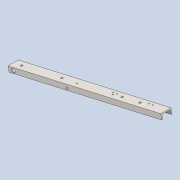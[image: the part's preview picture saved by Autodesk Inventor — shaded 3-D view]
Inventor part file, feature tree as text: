
AUTODESK INVENTOR PART (.ipt)
format: ipt  version: 2021 (Build 250183000, 183)  size: 134,144 bytes
history: native  units: mm
features: other x1, extrude x1, sketch x1, imported_body x1
ambient origin geometry x8: Origin, YZ Plane, XZ Plane, XY Plane, X Axis, Y Axis, Z Axis, Center Point
bodies: Body1 (feature_tree)
feature tree (4):
  other  "Sólido1"
  extrude  "Extrusión1"  TaperAngle=0.0deg  [1 undecoded]
  sketch  "Boceto1"  dims[d0=24.469mm d1=0.0mm d2=19.0mm d3=0.0mm d4=0.0mm]
  imported_body  "Base1"
note: 1 required parameter value undecoded (feature->parameter linkage not recoverable at this tier; creation-order binding heuristic only, values carry confidence <= 0.55)
